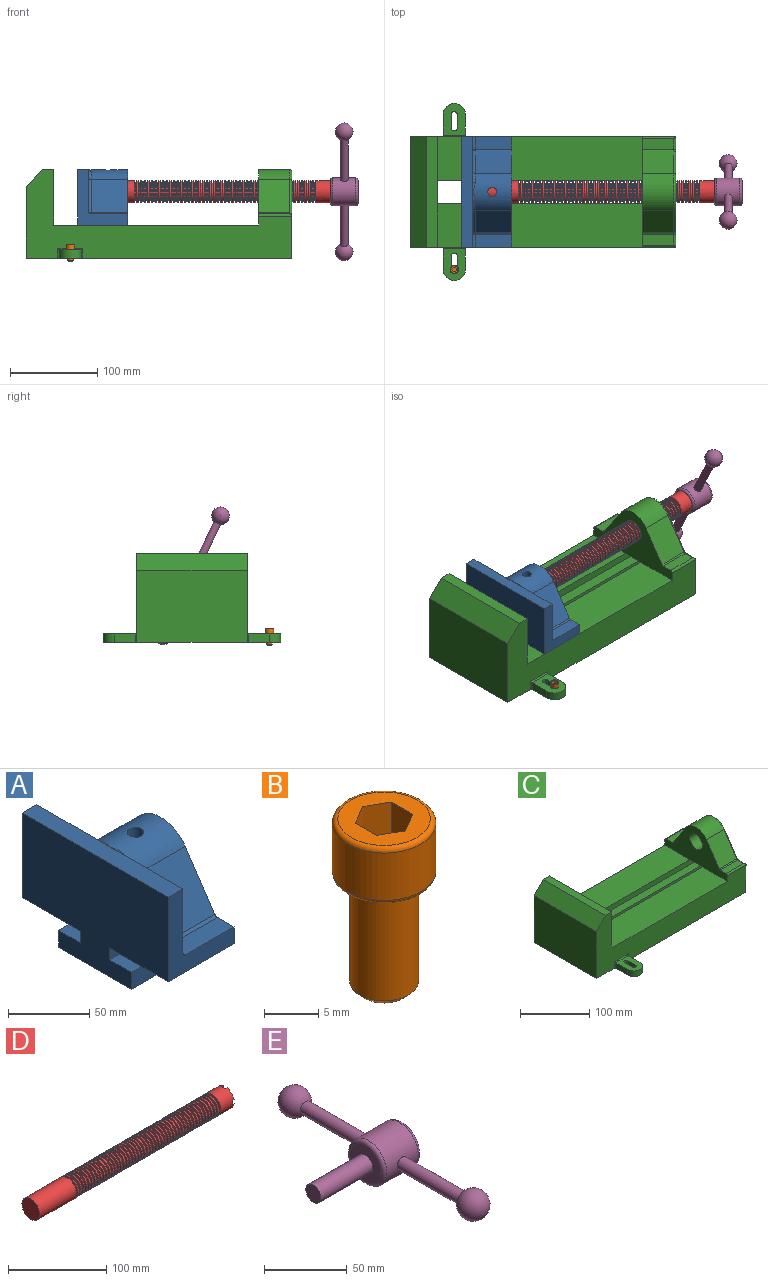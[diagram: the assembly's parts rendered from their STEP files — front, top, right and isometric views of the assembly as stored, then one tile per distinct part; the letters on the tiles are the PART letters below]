
ASSEMBLY  parts=5 mates=5
PART A: 36 faces, bbox 57.2x127x89 mm
  f0: plane 57.15x50.8mm, normal (0,0,-1), area 2903.2mm2, adj f6,f9,f10,f23
  f1: cylinder r=12.7mm len=44.45mm, axis (1,0,0), area 3464.3mm2, adj f6,f15,f16
  f2: plane 41.91x14.52mm, normal (0,0,1), area 608.5mm2, adj f6,f11,f24,f25
  f3: plane 51.86x48.26mm, normal (1,0,0), area 1495.7mm2, adj f8,f10,f31,f33,f35
  f4: plane 51.86x48.26mm, normal (1,0,0), area 1495.7mm2, adj f8,f11,f24,f28,f29
  f5: plane 57.15x50.8mm, normal (0,0,-1), area 2903.2mm2, adj f6,f9,f11,f22
  f6: plane 127x85.09mm, normal (1,0,0), area 5190.6mm2, adj f0,f1,f2,f5,f7,f10,f11,f12
  f7: plane 41.91x14.52mm, normal (0,0,1), area 608.5mm2, adj f6,f10,f30,f31
  f8: plane 127x12.7mm, normal (0,0,1), area 1612.9mm2, adj f3,f4,f9,f10,f11,f26,f34
  f9: plane 127x85.09mm, normal (-1,0,0), area 9096.8mm2, adj f0,f5,f8,f10,f11,f17,f18,f19
  f10: plane 63.5x57.15mm, normal (0,-1,0), area 1372.3mm2, adj f0,f3,f6,f7,f8,f9,f31
  f11: plane 63.5x57.15mm, normal (0,1,0), area 1372.3mm2, adj f2,f4,f5,f6,f8,f9,f24
  f12: plane 41.91x38.43mm, normal (0,-0.83,0.56), area 1939.2mm2, adj f6,f13,f30,f33
  f13: cylinder r=25.4mm len=44.45mm, axis (1,0,0), area 2026.5mm2, adj f6,f12,f14,f16,f26,f28,f34,f35
  f14: plane 41.91x38.43mm, normal (0,0.83,0.56), area 1939.2mm2, adj f6,f13,f25,f29
  f15: plane 25.4x25.4mm, normal (1,0,0), area 506.7mm2, adj f1
  f16: cylinder r=5.08mm len=13.76mm, axis (0,0,1), area 414mm2, adj f1,f13
  f17: plane 57.15x19.05mm, normal (0,0,1), area 1088.7mm2, adj f6,f9,f18,f23
  f18: plane 57.15x12.7mm, normal (0,-1,0), area 725.8mm2, adj f6,f9,f17,f19
  f19: plane 63.5x57.15mm, normal (0,0,-1), area 3629mm2, adj f6,f9,f18,f20
  f20: plane 57.15x12.7mm, normal (0,1,0), area 725.8mm2, adj f6,f9,f19,f21
  f21: plane 57.15x19.05mm, normal (0,0,1), area 1088.7mm2, adj f6,f9,f20,f22
  f22: plane 57.15x8.89mm, normal (0,1,0), area 508.1mm2, adj f5,f6,f9,f21
  f23: plane 57.15x8.89mm, normal (0,-1,0), area 508.1mm2, adj f0,f6,f9,f17
  f24: cylinder r=2.54mm len=14.52mm, axis (0,-1,0), area 57.9mm2, adj f2,f4,f11,f27
  f25: cylinder r=2.54mm len=41.91mm, axis (1,0,0), area 104.3mm2, adj f2,f6,f14,f27
  f26: bspline ~12.24x2.8mm, area 20.9mm2, adj f8,f13,f28
  f27: sphere r=2.54mm, area 6.3mm2, adj f24,f25,f29
  f28: torus R=27.94mm, axis (1,0,0), area 57.8mm2, adj f4,f13,f26,f29
  f29: cylinder r=2.54mm len=39.84mm, axis (0,-0.56,0.83), area 184.6mm2, adj f4,f14,f27,f28
  f30: cylinder r=2.54mm len=41.91mm, axis (1,0,0), area 104.3mm2, adj f6,f7,f12,f32
  f31: cylinder r=2.54mm len=14.52mm, axis (0,-1,0), area 57.9mm2, adj f3,f7,f10,f32
  f32: sphere r=2.54mm, area 6.3mm2, adj f30,f31,f33
  f33: cylinder r=2.54mm len=39.84mm, axis (0,-0.56,-0.83), area 184.6mm2, adj f3,f12,f32,f35
  f34: bspline ~12.24x2.8mm, area 20.9mm2, adj f8,f13,f35
  f35: torus R=27.94mm, axis (1,0,0), area 57.8mm2, adj f3,f13,f33,f34
PART B: 15 faces, bbox 10.3x10.3x19.1 mm
  f0: plane 8.51x8.51mm, normal (0,0,1), area 37.2mm2, adj f5,f6,f7,f8,f9,f10,f14
  f1: cylinder r=3.17mm len=11.94mm, axis (0,0,1), area 238.2mm2, adj f4,f12
  f2: plane 4.83x4.83mm, normal (0,0,-1), area 18.3mm2, adj f12
  f3: cylinder r=4.76mm len=9.53mm, axis (0,0,-1), area 159.6mm2, adj f13,f14
  f4: plane 8.51x8.51mm, normal (0,0,-1), area 25.2mm2, adj f1,f13
  f5: plane 4.83x2.38mm, normal (-0.5,-0.87,0), area 13.3mm2, adj f0,f6,f10,f11
  f6: plane 4.83x2.38mm, normal (0.5,-0.87,0), area 13.3mm2, adj f0,f5,f7,f11
  f7: plane 4.83x2.75mm, normal (1,0,0), area 13.3mm2, adj f0,f6,f8,f11
  f8: plane 4.83x2.38mm, normal (0.5,0.87,0), area 13.3mm2, adj f0,f7,f9,f11
  f9: plane 4.83x2.38mm, normal (-0.5,0.87,0), area 13.3mm2, adj f0,f8,f10,f11
  f10: plane 4.83x2.75mm, normal (-1,0,0), area 13.3mm2, adj f0,f5,f9,f11
  f11: plane 5.5x4.76mm, normal (0,0,1), area 19.6mm2, adj f5,f6,f7,f8,f9,f10
  f12: cone r=3.17mm half-angle=45deg, axis (0,0,1), area 18.9mm2, adj f1,f2
  f13: torus R=4.25mm, axis (0,0,1), area 23mm2, adj f3,f4
  f14: torus R=4.25mm, axis (0,0,1), area 23mm2, adj f0,f3
PART C: 61 faces, bbox 304.8x203.2x103.7 mm
  f0: plane 304.8x101.6mm, normal (0,1,0), area 13520.3mm2, adj f3,f4,f5,f6,f7,f8,f9,f16
  f1: plane 304.8x101.6mm, normal (0,-1,0), area 13520.3mm2, adj f2,f3,f5,f6,f7,f8,f9,f16
  f2: plane 234.95x50.8mm, normal (0,0,1), area 11935.5mm2, adj f1,f5,f16,f26
  f3: plane 127x99.06mm, normal (1,0,0), area 7097.5mm2, adj f0,f1,f9,f14,f17,f18,f19,f20
  f4: plane 234.95x50.8mm, normal (0,0,1), area 11935.5mm2, adj f0,f5,f16,f27
  f5: plane 127x101.6mm, normal (1,0,0), area 9516.1mm2, adj f0,f1,f2,f4,f6,f9,f18,f19
  f6: plane 127x12.7mm, normal (0,0,1), area 1612.9mm2, adj f0,f1,f5,f7
  f7: plane 127x19.05mm, normal (-0.71,0,0.71), area 3421.5mm2, adj f0,f1,f6,f8
  f8: plane 127x82.55mm, normal (-1,0,0), area 10483.8mm2, adj f0,f1,f7,f9
  f9: plane 304.8x203.2mm, normal (0,0,-1), area 33298.3mm2, adj f0,f1,f3,f5,f8,f21,f22,f39
  f10: plane 35.56x11.98mm, normal (0,0,1), area 426mm2, adj f16,f28,f29,f30
  f11: plane 38.43x35.56mm, normal (0,0.83,0.56), area 1645.4mm2, adj f12,f16,f29,f32
  f12: cylinder r=25.4mm len=42.19mm, axis (1,0,0), area 1770.2mm2, adj f11,f13,f16,f33
  f13: plane 38.43x35.56mm, normal (0,-0.83,0.56), area 1645.4mm2, adj f12,f16,f34,f35
  f14: cylinder r=12.7mm len=38.1mm, axis (1,0,0), area 3040.2mm2, adj f3,f16
  f15: plane 35.56x11.98mm, normal (0,0,1), area 426mm2, adj f16,f34,f36,f38
  f16: plane 127x63.5mm, normal (-1,0,0), area 4155.5mm2, adj f0,f1,f2,f4,f10,f11,f12,f13
  f17: plane 38.1x25.4mm, normal (0,0,-1), area 967.7mm2, adj f3,f16,f26,f27
  f18: plane 273.05x19.05mm, normal (0,0,-1), area 5201.6mm2, adj f3,f5,f19,f26
  f19: plane 273.05x12.7mm, normal (0,1,0), area 3467.7mm2, adj f3,f5,f18,f20
  f20: plane 273.05x19.05mm, normal (0,0,1), area 5201.6mm2, adj f3,f5,f19,f21
  f21: plane 273.05x16.51mm, normal (0,1,0), area 4508.1mm2, adj f3,f5,f9,f20
  f22: plane 273.05x16.51mm, normal (0,-1,0), area 4508.1mm2, adj f3,f5,f9,f23
  f23: plane 273.05x19.05mm, normal (0,0,1), area 5201.6mm2, adj f3,f5,f22,f24
  f24: plane 273.05x12.7mm, normal (0,-1,0), area 3467.7mm2, adj f3,f5,f23,f25
  f25: plane 273.05x19.05mm, normal (0,0,-1), area 5201.6mm2, adj f3,f5,f24,f27
  f26: plane 273.05x8.89mm, normal (0,1,0), area 2427.4mm2, adj f2,f3,f5,f17,f18
  f27: plane 273.05x8.89mm, normal (0,-1,0), area 2427.4mm2, adj f3,f4,f5,f17,f25
  f28: cylinder r=2.54mm len=38.1mm, axis (1,0,0), area 148.3mm2, adj f0,f10,f16,f30
  f29: cylinder r=2.54mm len=35.56mm, axis (-1,0,0), area 88.5mm2, adj f10,f11,f16,f31
  f30: cylinder r=2.54mm len=14.52mm, axis (0,1,0), area 54.3mm2, adj f3,f10,f28,f31
  f31: torus R=5.08mm, axis (-1,0,0), area 13.5mm2, adj f3,f29,f30,f32
  f32: cylinder r=2.54mm len=39.84mm, axis (0,0.56,-0.83), area 184.6mm2, adj f3,f11,f31,f33
  f33: torus R=22.86mm, axis (-1,0,0), area 191.4mm2, adj f3,f12,f32,f35
  f34: cylinder r=2.54mm len=35.56mm, axis (-1,0,0), area 88.5mm2, adj f13,f15,f16,f37
  f35: cylinder r=2.54mm len=39.84mm, axis (0,0.56,0.83), area 184.6mm2, adj f3,f13,f33,f37
  f36: cylinder r=2.54mm len=38.1mm, axis (-1,0,0), area 148.3mm2, adj f1,f15,f16,f38
  f37: torus R=5.08mm, axis (-1,0,0), area 13.5mm2, adj f3,f34,f35,f38
  f38: cylinder r=2.54mm len=14.52mm, axis (0,1,0), area 54.3mm2, adj f3,f15,f36,f37
  f39: plane 23.88x9.53mm, normal (-1,0,0), area 227.4mm2, adj f9,f45,f46,f60
  f40: plane 23.88x9.53mm, normal (1,0,0), area 227.4mm2, adj f9,f45,f46,f58
  f41: cylinder r=3.3mm len=9.53mm, axis (0,0,-1), area 98.8mm2, adj f9,f42,f44,f46
  f42: plane 15.62x9.53mm, normal (-1,0,0), area 148.8mm2, adj f9,f41,f43,f46
  f43: cylinder r=3.3mm len=9.53mm, axis (0,0,-1), area 98.8mm2, adj f9,f42,f44,f46
  f44: plane 15.62x9.53mm, normal (1,0,0), area 148.8mm2, adj f9,f41,f43,f46
  f45: cylinder r=12.7mm len=25.4mm, axis (0,0,-1), area 380mm2, adj f9,f39,f40,f46
  f46: plane 36.58x25.4mm, normal (0,0,1), area 722.4mm2, adj f39,f40,f41,f42,f43,f44,f45,f59
  f47: plane 23.88x9.53mm, normal (-1,0,0), area 227.4mm2, adj f9,f53,f54,f56
  f48: plane 23.88x9.53mm, normal (1,0,0), area 227.4mm2, adj f9,f53,f54,f55
  f49: cylinder r=3.3mm len=9.53mm, axis (0,0,-1), area 98.8mm2, adj f9,f50,f52,f54
  f50: plane 15.62x9.53mm, normal (-1,0,0), area 148.8mm2, adj f9,f49,f51,f54
  f51: cylinder r=3.3mm len=9.53mm, axis (0,0,-1), area 98.8mm2, adj f9,f50,f52,f54
  f52: plane 15.62x9.53mm, normal (1,0,0), area 148.8mm2, adj f9,f49,f51,f54
  f53: cylinder r=12.7mm len=25.4mm, axis (0,0,-1), area 380mm2, adj f9,f47,f48,f54
  f54: plane 36.58x25.4mm, normal (0,0,1), area 722.4mm2, adj f47,f48,f49,f50,f51,f52,f53,f57
  f55: cylinder r=1.52mm len=11.05mm, axis (0,0,-1), area 24.1mm2, adj f0,f9,f48,f57
  f56: cylinder r=1.52mm len=11.05mm, axis (0,0,1), area 24.1mm2, adj f0,f9,f47,f57
  f57: cylinder r=1.52mm len=28.45mm, axis (1,0,0), area 63.5mm2, adj f0,f54,f55,f56
  f58: cylinder r=1.52mm len=11.05mm, axis (0,0,1), area 24.1mm2, adj f1,f9,f40,f59
  f59: cylinder r=1.52mm len=28.45mm, axis (-1,0,0), area 63.5mm2, adj f1,f46,f58,f60
  f60: cylinder r=1.52mm len=11.05mm, axis (0,0,-1), area 24.1mm2, adj f1,f9,f39,f59
PART D: 220 faces, bbox 279.4x25.4x25.4 mm
  f0: cylinder r=12.7mm len=25.4mm, axis (-1,0,0), area 1468.2mm2, adj f1,f2,f3,f5,f7,f208,f209,f210
  f1: plane 9.9x9.9mm, normal (1,0,0), area 62.3mm2, adj f0,f4,f213,f216
  f2: plane 9.9x9.9mm, normal (1,0,0), area 62.3mm2, adj f0,f4,f210,f218
  f3: plane 9.9x9.9mm, normal (1,0,0), area 62.3mm2, adj f0,f4,f209,f212
  f4: cylinder r=6.35mm len=25.4mm, axis (1,0,0), area 960.3mm2, adj f1,f2,f3,f5,f6,f208,f209,f210
  f5: plane 9.9x9.9mm, normal (1,0,0), area 62.3mm2, adj f0,f4,f215,f217
  f6: plane 12.7x12.7mm, normal (1,0,0), area 126.7mm2, adj f4
  f7: cone r=12.7mm half-angle=76deg, axis (1,0,0), area 188mm2, adj f0,f9
  f8: cone r=10.16mm half-angle=76deg, axis (-1,0,0), area 188mm2, adj f9,f10
  f9: cylinder r=10.16mm len=20.32mm, axis (1,0,0), area 81.1mm2, adj f7,f8
  f10: cylinder r=12.7mm len=25.4mm, axis (-1,0,0), area 131.7mm2, adj f8,f11
  f11: cone r=12.7mm half-angle=76deg, axis (1,0,0), area 188mm2, adj f10,f13
  f12: cone r=10.16mm half-angle=76deg, axis (-1,0,0), area 188mm2, adj f13,f14
  f13: cylinder r=10.16mm len=20.32mm, axis (1,0,0), area 81.1mm2, adj f11,f12
  f14: cylinder r=12.7mm len=25.4mm, axis (-1,0,0), area 131.7mm2, adj f12,f15
  f15: cone r=12.7mm half-angle=76deg, axis (1,0,0), area 188mm2, adj f14,f17
  f16: cone r=10.16mm half-angle=76deg, axis (-1,0,0), area 188mm2, adj f17,f18
  f17: cylinder r=10.16mm len=20.32mm, axis (1,0,0), area 81.1mm2, adj f15,f16
  f18: cylinder r=12.7mm len=25.4mm, axis (-1,0,0), area 131.7mm2, adj f16,f19
  f19: cone r=12.7mm half-angle=76deg, axis (1,0,0), area 188mm2, adj f18,f21
  f20: cone r=10.16mm half-angle=76deg, axis (-1,0,0), area 188mm2, adj f21,f22
  f21: cylinder r=10.16mm len=20.32mm, axis (1,0,0), area 81.1mm2, adj f19,f20
  f22: cylinder r=12.7mm len=25.4mm, axis (-1,0,0), area 131.7mm2, adj f20,f23
  f23: cone r=12.7mm half-angle=76deg, axis (1,0,0), area 188mm2, adj f22,f25
  f24: cone r=10.16mm half-angle=76deg, axis (-1,0,0), area 188mm2, adj f25,f26
  f25: cylinder r=10.16mm len=20.32mm, axis (1,0,0), area 81.1mm2, adj f23,f24
  f26: cylinder r=12.7mm len=25.4mm, axis (-1,0,0), area 131.7mm2, adj f24,f27
  f27: cone r=12.7mm half-angle=76deg, axis (1,0,0), area 188mm2, adj f26,f29
  f28: cone r=10.16mm half-angle=76deg, axis (-1,0,0), area 188mm2, adj f29,f30
  f29: cylinder r=10.16mm len=20.32mm, axis (1,0,0), area 81.1mm2, adj f27,f28
  f30: cylinder r=12.7mm len=25.4mm, axis (-1,0,0), area 131.7mm2, adj f28,f31
  f31: cone r=12.7mm half-angle=76deg, axis (1,0,0), area 188mm2, adj f30,f33
  f32: cone r=10.16mm half-angle=76deg, axis (-1,0,0), area 188mm2, adj f33,f34
  f33: cylinder r=10.16mm len=20.32mm, axis (1,0,0), area 81.1mm2, adj f31,f32
  f34: cylinder r=12.7mm len=25.4mm, axis (-1,0,0), area 131.7mm2, adj f32,f35
  f35: cone r=12.7mm half-angle=76deg, axis (1,0,0), area 188mm2, adj f34,f37
  f36: cone r=10.16mm half-angle=76deg, axis (-1,0,0), area 188mm2, adj f37,f38
  f37: cylinder r=10.16mm len=20.32mm, axis (1,0,0), area 81.1mm2, adj f35,f36
  f38: cylinder r=12.7mm len=25.4mm, axis (-1,0,0), area 131.7mm2, adj f36,f39
  f39: cone r=12.7mm half-angle=76deg, axis (1,0,0), area 188mm2, adj f38,f41
  f40: cone r=10.16mm half-angle=76deg, axis (-1,0,0), area 188mm2, adj f41,f42
  f41: cylinder r=10.16mm len=20.32mm, axis (1,0,0), area 81.1mm2, adj f39,f40
  f42: cylinder r=12.7mm len=25.4mm, axis (-1,0,0), area 131.7mm2, adj f40,f43
  f43: cone r=12.7mm half-angle=76deg, axis (1,0,0), area 188mm2, adj f42,f45
  f44: cone r=10.16mm half-angle=76deg, axis (-1,0,0), area 188mm2, adj f45,f46
  f45: cylinder r=10.16mm len=20.32mm, axis (1,0,0), area 81.1mm2, adj f43,f44
  f46: cylinder r=12.7mm len=25.4mm, axis (-1,0,0), area 131.7mm2, adj f44,f47
  f47: cone r=12.7mm half-angle=76deg, axis (1,0,0), area 188mm2, adj f46,f49
  f48: cone r=10.16mm half-angle=76deg, axis (-1,0,0), area 188mm2, adj f49,f50
  f49: cylinder r=10.16mm len=20.32mm, axis (1,0,0), area 81.1mm2, adj f47,f48
  f50: cylinder r=12.7mm len=25.4mm, axis (-1,0,0), area 131.7mm2, adj f48,f51
  f51: cone r=12.7mm half-angle=76deg, axis (1,0,0), area 188mm2, adj f50,f53
  f52: cone r=10.16mm half-angle=76deg, axis (-1,0,0), area 188mm2, adj f53,f54
  f53: cylinder r=10.16mm len=20.32mm, axis (1,0,0), area 81.1mm2, adj f51,f52
  f54: cylinder r=12.7mm len=25.4mm, axis (-1,0,0), area 131.7mm2, adj f52,f55
  f55: cone r=12.7mm half-angle=76deg, axis (1,0,0), area 188mm2, adj f54,f57
  f56: cone r=10.16mm half-angle=76deg, axis (-1,0,0), area 188mm2, adj f57,f58
  f57: cylinder r=10.16mm len=20.32mm, axis (1,0,0), area 81.1mm2, adj f55,f56
  f58: cylinder r=12.7mm len=25.4mm, axis (-1,0,0), area 131.7mm2, adj f56,f59
  f59: cone r=12.7mm half-angle=76deg, axis (1,0,0), area 188mm2, adj f58,f61
  f60: cone r=10.16mm half-angle=76deg, axis (-1,0,0), area 188mm2, adj f61,f62
  f61: cylinder r=10.16mm len=20.32mm, axis (1,0,0), area 81.1mm2, adj f59,f60
  f62: cylinder r=12.7mm len=25.4mm, axis (-1,0,0), area 131.7mm2, adj f60,f63
  f63: cone r=12.7mm half-angle=76deg, axis (1,0,0), area 188mm2, adj f62,f65
  f64: cone r=10.16mm half-angle=76deg, axis (-1,0,0), area 188mm2, adj f65,f66
  f65: cylinder r=10.16mm len=20.32mm, axis (1,0,0), area 81.1mm2, adj f63,f64
  f66: cylinder r=12.7mm len=25.4mm, axis (-1,0,0), area 131.7mm2, adj f64,f67
  f67: cone r=12.7mm half-angle=76deg, axis (1,0,0), area 188mm2, adj f66,f69
  f68: cone r=10.16mm half-angle=76deg, axis (-1,0,0), area 188mm2, adj f69,f70
  f69: cylinder r=10.16mm len=20.32mm, axis (1,0,0), area 81.1mm2, adj f67,f68
  f70: cylinder r=12.7mm len=25.4mm, axis (-1,0,0), area 131.7mm2, adj f68,f71
  f71: cone r=12.7mm half-angle=76deg, axis (1,0,0), area 188mm2, adj f70,f73
  f72: cone r=10.16mm half-angle=76deg, axis (-1,0,0), area 188mm2, adj f73,f74
  f73: cylinder r=10.16mm len=20.32mm, axis (1,0,0), area 81.1mm2, adj f71,f72
  f74: cylinder r=12.7mm len=25.4mm, axis (-1,0,0), area 131.7mm2, adj f72,f75
  f75: cone r=12.7mm half-angle=76deg, axis (1,0,0), area 188mm2, adj f74,f77
  f76: cone r=10.16mm half-angle=76deg, axis (-1,0,0), area 188mm2, adj f77,f78
  f77: cylinder r=10.16mm len=20.32mm, axis (1,0,0), area 81.1mm2, adj f75,f76
  f78: cylinder r=12.7mm len=25.4mm, axis (-1,0,0), area 131.7mm2, adj f76,f79
  f79: cone r=12.7mm half-angle=76deg, axis (1,0,0), area 188mm2, adj f78,f81
  f80: cone r=10.16mm half-angle=76deg, axis (-1,0,0), area 188mm2, adj f81,f82
  f81: cylinder r=10.16mm len=20.32mm, axis (1,0,0), area 81.1mm2, adj f79,f80
  f82: cylinder r=12.7mm len=25.4mm, axis (-1,0,0), area 131.7mm2, adj f80,f83
  f83: cone r=12.7mm half-angle=76deg, axis (1,0,0), area 188mm2, adj f82,f85
  f84: cone r=10.16mm half-angle=76deg, axis (-1,0,0), area 188mm2, adj f85,f86
  f85: cylinder r=10.16mm len=20.32mm, axis (1,0,0), area 81.1mm2, adj f83,f84
  f86: cylinder r=12.7mm len=25.4mm, axis (-1,0,0), area 131.7mm2, adj f84,f87
  f87: cone r=12.7mm half-angle=76deg, axis (1,0,0), area 188mm2, adj f86,f89
  f88: cone r=10.16mm half-angle=76deg, axis (-1,0,0), area 188mm2, adj f89,f90
  f89: cylinder r=10.16mm len=20.32mm, axis (1,0,0), area 81.1mm2, adj f87,f88
  f90: cylinder r=12.7mm len=25.4mm, axis (-1,0,0), area 131.7mm2, adj f88,f91
  f91: cone r=12.7mm half-angle=76deg, axis (1,0,0), area 188mm2, adj f90,f93
  f92: cone r=10.16mm half-angle=76deg, axis (-1,0,0), area 188mm2, adj f93,f94
  f93: cylinder r=10.16mm len=20.32mm, axis (1,0,0), area 81.1mm2, adj f91,f92
  f94: cylinder r=12.7mm len=25.4mm, axis (-1,0,0), area 131.7mm2, adj f92,f95
  f95: cone r=12.7mm half-angle=76deg, axis (1,0,0), area 188mm2, adj f94,f97
  f96: cone r=10.16mm half-angle=76deg, axis (-1,0,0), area 188mm2, adj f97,f98
  f97: cylinder r=10.16mm len=20.32mm, axis (1,0,0), area 81.1mm2, adj f95,f96
  f98: cylinder r=12.7mm len=25.4mm, axis (-1,0,0), area 131.7mm2, adj f96,f99
  f99: cone r=12.7mm half-angle=76deg, axis (1,0,0), area 188mm2, adj f98,f101
  f100: cone r=10.16mm half-angle=76deg, axis (-1,0,0), area 188mm2, adj f101,f102
  f101: cylinder r=10.16mm len=20.32mm, axis (1,0,0), area 81.1mm2, adj f99,f100
  f102: cylinder r=12.7mm len=25.4mm, axis (-1,0,0), area 131.7mm2, adj f100,f103
  f103: cone r=12.7mm half-angle=76deg, axis (1,0,0), area 188mm2, adj f102,f105
  f104: cone r=10.16mm half-angle=76deg, axis (-1,0,0), area 188mm2, adj f105,f106
  f105: cylinder r=10.16mm len=20.32mm, axis (1,0,0), area 81.1mm2, adj f103,f104
  f106: cylinder r=12.7mm len=25.4mm, axis (-1,0,0), area 131.7mm2, adj f104,f107
  f107: cone r=12.7mm half-angle=76deg, axis (1,0,0), area 188mm2, adj f106,f109
  f108: cone r=10.16mm half-angle=76deg, axis (-1,0,0), area 188mm2, adj f109,f110
  f109: cylinder r=10.16mm len=20.32mm, axis (1,0,0), area 81.1mm2, adj f107,f108
  f110: cylinder r=12.7mm len=25.4mm, axis (-1,0,0), area 131.7mm2, adj f108,f111
  f111: cone r=12.7mm half-angle=76deg, axis (1,0,0), area 188mm2, adj f110,f113
  f112: cone r=10.16mm half-angle=76deg, axis (-1,0,0), area 188mm2, adj f113,f114
  f113: cylinder r=10.16mm len=20.32mm, axis (1,0,0), area 81.1mm2, adj f111,f112
  f114: cylinder r=12.7mm len=25.4mm, axis (-1,0,0), area 131.7mm2, adj f112,f115
  f115: cone r=12.7mm half-angle=76deg, axis (1,0,0), area 188mm2, adj f114,f117
  f116: cone r=10.16mm half-angle=76deg, axis (-1,0,0), area 188mm2, adj f117,f118
  f117: cylinder r=10.16mm len=20.32mm, axis (1,0,0), area 81.1mm2, adj f115,f116
  f118: cylinder r=12.7mm len=25.4mm, axis (-1,0,0), area 131.7mm2, adj f116,f119
  f119: cone r=12.7mm half-angle=76deg, axis (1,0,0), area 188mm2, adj f118,f121
  f120: cone r=10.16mm half-angle=76deg, axis (-1,0,0), area 188mm2, adj f121,f122
  f121: cylinder r=10.16mm len=20.32mm, axis (1,0,0), area 81.1mm2, adj f119,f120
  f122: cylinder r=12.7mm len=25.4mm, axis (-1,0,0), area 131.7mm2, adj f120,f123
  f123: cone r=12.7mm half-angle=76deg, axis (1,0,0), area 188mm2, adj f122,f125
  f124: cone r=10.16mm half-angle=76deg, axis (-1,0,0), area 188mm2, adj f125,f126
  f125: cylinder r=10.16mm len=20.32mm, axis (1,0,0), area 81.1mm2, adj f123,f124
  f126: cylinder r=12.7mm len=25.4mm, axis (-1,0,0), area 131.7mm2, adj f124,f127
  f127: cone r=12.7mm half-angle=76deg, axis (1,0,0), area 188mm2, adj f126,f129
  f128: cone r=10.16mm half-angle=76deg, axis (-1,0,0), area 188mm2, adj f129,f130
  f129: cylinder r=10.16mm len=20.32mm, axis (1,0,0), area 81.1mm2, adj f127,f128
  f130: cylinder r=12.7mm len=25.4mm, axis (-1,0,0), area 131.7mm2, adj f128,f131
  f131: cone r=12.7mm half-angle=76deg, axis (1,0,0), area 188mm2, adj f130,f133
  f132: cone r=10.16mm half-angle=76deg, axis (-1,0,0), area 188mm2, adj f133,f134
  f133: cylinder r=10.16mm len=20.32mm, axis (1,0,0), area 81.1mm2, adj f131,f132
  f134: cylinder r=12.7mm len=25.4mm, axis (-1,0,0), area 131.7mm2, adj f132,f135
  f135: cone r=12.7mm half-angle=76deg, axis (1,0,0), area 188mm2, adj f134,f137
  f136: cone r=10.16mm half-angle=76deg, axis (-1,0,0), area 188mm2, adj f137,f138
  f137: cylinder r=10.16mm len=20.32mm, axis (1,0,0), area 81.1mm2, adj f135,f136
  f138: cylinder r=12.7mm len=25.4mm, axis (-1,0,0), area 131.7mm2, adj f136,f139
  f139: cone r=12.7mm half-angle=76deg, axis (1,0,0), area 188mm2, adj f138,f141
  f140: cone r=10.16mm half-angle=76deg, axis (-1,0,0), area 188mm2, adj f141,f142
  f141: cylinder r=10.16mm len=20.32mm, axis (1,0,0), area 81.1mm2, adj f139,f140
  f142: cylinder r=12.7mm len=25.4mm, axis (-1,0,0), area 131.7mm2, adj f140,f143
  f143: cone r=12.7mm half-angle=76deg, axis (1,0,0), area 188mm2, adj f142,f145
  f144: cone r=10.16mm half-angle=76deg, axis (-1,0,0), area 188mm2, adj f145,f146
  f145: cylinder r=10.16mm len=20.32mm, axis (1,0,0), area 81.1mm2, adj f143,f144
  f146: cylinder r=12.7mm len=25.4mm, axis (-1,0,0), area 131.7mm2, adj f144,f147
  f147: cone r=12.7mm half-angle=76deg, axis (1,0,0), area 188mm2, adj f146,f149
  f148: cone r=10.16mm half-angle=76deg, axis (-1,0,0), area 188mm2, adj f149,f150
  f149: cylinder r=10.16mm len=20.32mm, axis (1,0,0), area 81.1mm2, adj f147,f148
  f150: cylinder r=12.7mm len=25.4mm, axis (-1,0,0), area 131.7mm2, adj f148,f151
  f151: cone r=12.7mm half-angle=76deg, axis (1,0,0), area 188mm2, adj f150,f153
  f152: cone r=10.16mm half-angle=76deg, axis (-1,0,0), area 188mm2, adj f153,f154
  f153: cylinder r=10.16mm len=20.32mm, axis (1,0,0), area 81.1mm2, adj f151,f152
  f154: cylinder r=12.7mm len=25.4mm, axis (-1,0,0), area 131.7mm2, adj f152,f155
  f155: cone r=12.7mm half-angle=76deg, axis (1,0,0), area 188mm2, adj f154,f157
  f156: cone r=10.16mm half-angle=76deg, axis (-1,0,0), area 188mm2, adj f157,f158
  f157: cylinder r=10.16mm len=20.32mm, axis (1,0,0), area 81.1mm2, adj f155,f156
  f158: cylinder r=12.7mm len=25.4mm, axis (-1,0,0), area 131.7mm2, adj f156,f159
  f159: cone r=12.7mm half-angle=76deg, axis (1,0,0), area 188mm2, adj f158,f161
  f160: cone r=10.16mm half-angle=76deg, axis (-1,0,0), area 188mm2, adj f161,f162
  f161: cylinder r=10.16mm len=20.32mm, axis (1,0,0), area 81.1mm2, adj f159,f160
  f162: cylinder r=12.7mm len=25.4mm, axis (-1,0,0), area 131.7mm2, adj f160,f163
  f163: cone r=12.7mm half-angle=76deg, axis (1,0,0), area 188mm2, adj f162,f165
  f164: cone r=10.16mm half-angle=76deg, axis (-1,0,0), area 188mm2, adj f165,f166
  f165: cylinder r=10.16mm len=20.32mm, axis (1,0,0), area 81.1mm2, adj f163,f164
  f166: cylinder r=12.7mm len=25.4mm, axis (-1,0,0), area 131.7mm2, adj f164,f167
  f167: cone r=12.7mm half-angle=76deg, axis (1,0,0), area 188mm2, adj f166,f169
  f168: cone r=10.16mm half-angle=76deg, axis (-1,0,0), area 188mm2, adj f169,f170
  f169: cylinder r=10.16mm len=20.32mm, axis (1,0,0), area 81.1mm2, adj f167,f168
  f170: cylinder r=12.7mm len=25.4mm, axis (-1,0,0), area 131.7mm2, adj f168,f171
  f171: cone r=12.7mm half-angle=76deg, axis (1,0,0), area 188mm2, adj f170,f173
  f172: cone r=10.16mm half-angle=76deg, axis (-1,0,0), area 188mm2, adj f173,f174
  f173: cylinder r=10.16mm len=20.32mm, axis (1,0,0), area 81.1mm2, adj f171,f172
  f174: cylinder r=12.7mm len=25.4mm, axis (-1,0,0), area 131.7mm2, adj f172,f175
  f175: cone r=12.7mm half-angle=76deg, axis (1,0,0), area 188mm2, adj f174,f177
  f176: cone r=10.16mm half-angle=76deg, axis (-1,0,0), area 188mm2, adj f177,f178
  f177: cylinder r=10.16mm len=20.32mm, axis (1,0,0), area 81.1mm2, adj f175,f176
  f178: cylinder r=12.7mm len=25.4mm, axis (-1,0,0), area 131.7mm2, adj f176,f179
  f179: cone r=12.7mm half-angle=76deg, axis (1,0,0), area 188mm2, adj f178,f181
  f180: cone r=10.16mm half-angle=76deg, axis (-1,0,0), area 188mm2, adj f181,f182
  f181: cylinder r=10.16mm len=20.32mm, axis (1,0,0), area 81.1mm2, adj f179,f180
  f182: cylinder r=12.7mm len=25.4mm, axis (-1,0,0), area 131.7mm2, adj f180,f183
  f183: cone r=12.7mm half-angle=76deg, axis (1,0,0), area 188mm2, adj f182,f185
  f184: cone r=10.16mm half-angle=76deg, axis (-1,0,0), area 188mm2, adj f185,f186
  f185: cylinder r=10.16mm len=20.32mm, axis (1,0,0), area 81.1mm2, adj f183,f184
  f186: cylinder r=12.7mm len=25.4mm, axis (-1,0,0), area 131.7mm2, adj f184,f187
  f187: cone r=12.7mm half-angle=76deg, axis (1,0,0), area 188mm2, adj f186,f189
  f188: cone r=10.16mm half-angle=76deg, axis (-1,0,0), area 188mm2, adj f189,f190
  f189: cylinder r=10.16mm len=20.32mm, axis (1,0,0), area 81.1mm2, adj f187,f188
  f190: cylinder r=12.7mm len=25.4mm, axis (-1,0,0), area 131.7mm2, adj f188,f191
  f191: cone r=12.7mm half-angle=76deg, axis (1,0,0), area 188mm2, adj f190,f193
  f192: cone r=10.16mm half-angle=76deg, axis (-1,0,0), area 188mm2, adj f193,f194
  f193: cylinder r=10.16mm len=20.32mm, axis (1,0,0), area 81.1mm2, adj f191,f192
  f194: cylinder r=12.7mm len=25.4mm, axis (-1,0,0), area 131.7mm2, adj f192,f195
  f195: cone r=12.7mm half-angle=76deg, axis (1,0,0), area 188mm2, adj f194,f197
  f196: cone r=10.16mm half-angle=76deg, axis (-1,0,0), area 188mm2, adj f197,f198
  f197: cylinder r=10.16mm len=20.32mm, axis (1,0,0), area 81.1mm2, adj f195,f196
  f198: cylinder r=12.7mm len=25.4mm, axis (-1,0,0), area 131.7mm2, adj f196,f199
  f199: cone r=12.7mm half-angle=76deg, axis (1,0,0), area 188mm2, adj f198,f201
  f200: cone r=10.16mm half-angle=76deg, axis (-1,0,0), area 188mm2, adj f201,f202
  f201: cylinder r=10.16mm len=20.32mm, axis (1,0,0), area 81.1mm2, adj f199,f200
  f202: cylinder r=12.7mm len=25.4mm, axis (-1,0,0), area 131.7mm2, adj f200,f203
  f203: cone r=12.7mm half-angle=76deg, axis (1,0,0), area 188mm2, adj f202,f205
  f204: cone r=10.16mm half-angle=76deg, axis (-1,0,0), area 188mm2, adj f205,f207
  f205: cylinder r=10.16mm len=20.32mm, axis (1,0,0), area 81.1mm2, adj f203,f204
  f206: plane 25.4x25.4mm, normal (-1,0,0), area 506.7mm2, adj f207
  f207: cylinder r=12.7mm len=52.45mm, axis (-1,0,0), area 4185.4mm2, adj f204,f206
  f208: plane 6.88x5.08mm, normal (1,0,0), area 32.7mm2, adj f0,f4,f209,f210
  f209: plane 6.62x2.54mm, normal (0,-1,0), area 16.8mm2, adj f0,f3,f4,f208
  f210: plane 6.62x2.54mm, normal (0,1,0), area 16.8mm2, adj f0,f2,f4,f208
  f211: plane 6.88x5.08mm, normal (1,0,0), area 32.7mm2, adj f0,f4,f212,f213
  f212: plane 6.62x2.54mm, normal (0,0,1), area 16.8mm2, adj f0,f3,f4,f211
  f213: plane 6.62x2.54mm, normal (0,0,-1), area 16.8mm2, adj f0,f1,f4,f211
  f214: plane 6.88x5.08mm, normal (1,0,0), area 32.7mm2, adj f0,f4,f215,f216
  f215: plane 6.62x2.54mm, normal (0,1,0), area 16.8mm2, adj f0,f4,f5,f214
  f216: plane 6.62x2.54mm, normal (0,-1,0), area 16.8mm2, adj f0,f1,f4,f214
  f217: plane 6.62x2.54mm, normal (0,0,-1), area 16.8mm2, adj f0,f4,f5,f219
  f218: plane 6.62x2.54mm, normal (0,0,1), area 16.8mm2, adj f0,f2,f4,f219
  f219: plane 6.88x5.08mm, normal (1,0,0), area 32.7mm2, adj f0,f4,f217,f218
PART E: 11 faces, bbox 76.2x172.7x34.4 mm
  f0: sphere r=10.16mm, area 1231.8mm2, adj f1
  f1: cylinder r=4.45mm len=51.82mm, axis (0,1,0), area 1438.5mm2, adj f0,f4
  f2: sphere r=10.16mm, area 1231.8mm2, adj f3
  f3: cylinder r=4.45mm len=51.82mm, axis (0,1,0), area 1438.5mm2, adj f2,f4
  f4: cylinder r=15.88mm len=31.75mm, axis (-1,0,0), area 2534.7mm2, adj f1,f3,f9,f10
  f5: cylinder r=6.35mm len=44.45mm, axis (-1,0,0), area 1773.5mm2, adj f6,f8
  f6: plane 12.7x12.7mm, normal (-1,0,0), area 126.7mm2, adj f5
  f7: plane 26.67x26.67mm, normal (1,0,0), area 558.6mm2, adj f10
  f8: plane 26.67x26.67mm, normal (-1,0,0), area 432mm2, adj f5,f9
  f9: torus R=13.33mm, axis (1,0,0), area 374.8mm2, adj f4,f8
  f10: torus R=13.33mm, axis (1,0,0), area 374.8mm2, adj f4,f7
PLACE A t=(27.68,0,0)mm
PLACE B rot(axis=(0,0,1),90deg) t=(-254,-88.9,9.52)mm
PLACE C at identity fixed
PLACE D rot(axis=(1,0,0),115.4deg) t=(27.68,68.82,108.91)mm
PLACE E rot(axis=(1,0,0),115.4deg) t=(6.09,68.82,108.91)mm
MATE fastened D.f4 <-> E.f5  axis (1,0,0) through (44.19,0,76.2)mm
MATE planar A.f0 <-> C.f2  axis (0,0,-1) through (-216.8,-38.1,38.1)mm
MATE pin_slot B.f1 <-> C.f41  axis (0,0,1) through (-254,-88.9,9.52)mm
MATE revolute D.f7 <-> A.f28  axis (-1,0,0) through (-232.67,0,76.2)mm
MATE cylindrical C.f12 <-> D.f7  axis (-1,0,0) through (-38.1,0,76.2)mm
